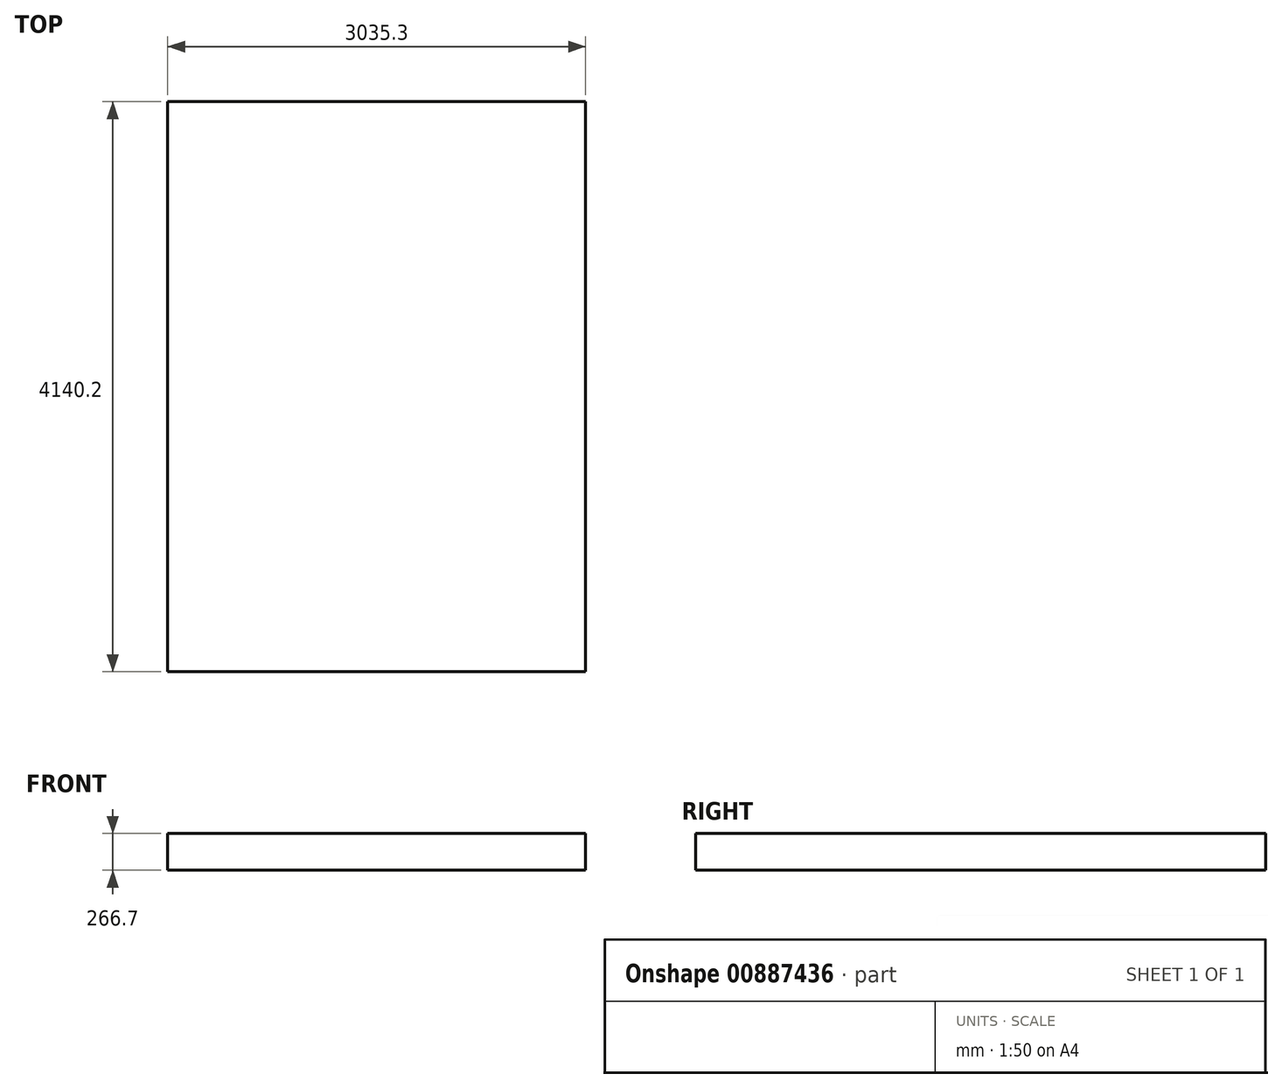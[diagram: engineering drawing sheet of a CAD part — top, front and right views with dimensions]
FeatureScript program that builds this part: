
annotation { "Feature Type Name" : "Feature", "Feature Type Description" : "" }
export const myFeature = defineFeature(function(context is Context, id is Id, definition is map)
    precondition{}
    {
        {
            var Q0;
            Q0=qCreatedBy(makeId("Top.planeOp"),FACE);
            var sketch = newSketch(context, id + "F0", { "sketchPlane" : qUnion([Q0])});
            skLineSegment(sketch, "E0.bottom", {"start": v(-59.45, 4055.36) * mm, "end": v(2975.85, 4055.36) * mm});
            skLineSegment(sketch, "E0.top", {"start": v(-59.45, -84.84) * mm, "end": v(2975.85, -84.84) * mm});
            skLineSegment(sketch, "E0.left", {"start": v(-59.45, 4055.36) * mm, "end": v(-59.45, -84.84) * mm});
            skLineSegment(sketch, "E0.right", {"start": v(2975.85, 4055.36) * mm, "end": v(2975.85, -84.84) * mm});
            skSolve(sketch);
        }
        {
            var Q0;
            Q0 = qSketchRegion(id + "F0", true);
            extrude(context, id + "F1", {"entities" : qUnion([Q0]), "depth" : 266.7 * mm, "offsetDistance" : 25 * mm});
        }
    });
